# Revit family: Haworth_Intuity_Parkbench_HighTable_EU_PRELIMINARY
name_source: partatom
category: Furniture
units: mm (PartAtom-declared; Revit-internal decimal feet)

## family parameters
Always vertical = Yes
Cut with Voids When Loaded = No
OmniClass Number = 23.40.20.00
OmniClass Title = General Furniture and Specialties
Room Calculation Point = No
Shared = No
Work Plane-Based = No

## types (8) — shared parameters
Actual Height = 105 cm
Assembly Code = E2020200
Casters = Yes
Cord Height = 41 cm
Description = Haworth - Intuity - Parkbench - High Table
Glide Finish = Haworth _ Paint _ Allways Black
Glide Height = 9 cm
Glides = No
Manufacturer = Haworth
Max. Depth = 140 cm
Max. Width = 240 cm
Min. Depth = 100 cm
Min. Width = 160 cm
Model = PBHTXXXX
Size = Verify Final Dim. w/ Haworth
Tray Finish = Haworth _ Paint _ Allways White TROWC
URL = https://www.haworth.com
URL - Product = https://www.haworth.com
Version = 1
Warranty = http://www.haworth.com
With Top = Yes
with Cord = Yes

## per-type parameters (varying)
| type | Actual Depth | Actual Width | Depth | Metal Foot Rest | Metal Foot Rest w Cover | Tray Width | Width | Wood Offset | w/o Foot Rest |
| 240 x 140 - w Metal Foot Rest w Cover | 140 cm | 240 cm | 140 cm | No | Yes | 150 cm | 240 cm | 60 cm | No |
| 200 x 140 - w Metal Foot Rest w Cover | 140 cm | 200 cm | 140 cm | No | Yes | 110 cm | 200 cm | 50 cm | No |
| 240 x 120 - w Metal Foot Rest | 120 cm | 240 cm | 120 cm | Yes | No | 150 cm | 240 cm | 60 cm | No |
| 200 x 120 - w Metal Foot Rest | 120 cm | 200 cm | 120 cm | Yes | No | 110 cm | 200 cm | 50 cm | No |
| 240 x 100 - w/o Foot Rest | 100 cm | 240 cm | 100 cm | No | No | 150 cm | 240 cm | 60 cm | Yes |
| 200 x 100 - w/o Foot Rest | 100 cm | 200 cm | 100 cm | No | No | 110 cm | 200 cm | 50 cm | Yes |
| 180 x 100 - w Metal Foot Rest w Cover | 100 cm | 180 cm | 100 cm | No | Yes | 90 cm | 180 cm | 45 cm | No |
| 160 x 100 - w Metal Foot Rest | 100 cm | 160 cm | 100 cm | Yes | No | 70 cm | 160 cm | 40 cm | No |

## geometry (parser evidence)
native form markers: Sweep x9
no freeform markers — native parametric forms only
